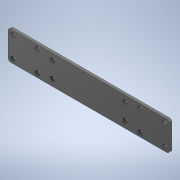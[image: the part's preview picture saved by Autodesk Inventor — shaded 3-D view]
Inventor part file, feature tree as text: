
AUTODESK INVENTOR PART (.ipt)
format: ipt  version: 2020 (Build 240168000, 168)  size: 157,184 bytes
history: native  units: mm
features: sketch x3, extrude x2, fillet x1, hole x1
ambient origin geometry x8: Origin, YZ Plane, XZ Plane, XY Plane, X Axis, Y Axis, Z Axis, Center Point
bodies: Solid1 (feature_tree)
feature tree (7):
  extrude  "Extrusion1"  Depth=36.0mm
  extrude  "Extrusion2"  Depth=3.0mm
  fillet  "Fillet1"  Radius=26.0mm
  hole  "Hole1"  [1 undecoded]
  sketch  "Sketch1"  dims[d0=200.0mm d1=36.0mm]
  sketch  "Sketch2"  dims[d2=3.0mm d3=0.0mm d4=30.5mm d5=26.0mm]
  sketch  "Sketch3"  dims[d6=42.0mm d7=0.0mm d8=0.0mm d9=5.5mm d10=5.5mm d11=5.5mm d12=5.5mm d13=30.5mm d14=26.0mm d15=42.0mm d16=0.0mm d17=5.5mm d18=5.5mm d19=5.5mm d20=5.5mm d21=0.0mm d22=36.0mm d23=3.0mm d24=0.0mm d25=3.0mm d26=90.0mm d27=20.0mm d28=5.5mm d29=6.0mm d30=4.0mm d31=2.0mm d32=90.0deg d33=8.0mm d34=20.594885mm]
note: 1 required parameter value undecoded (feature->parameter linkage not recoverable at this tier; creation-order binding heuristic only, values carry confidence <= 0.55)
